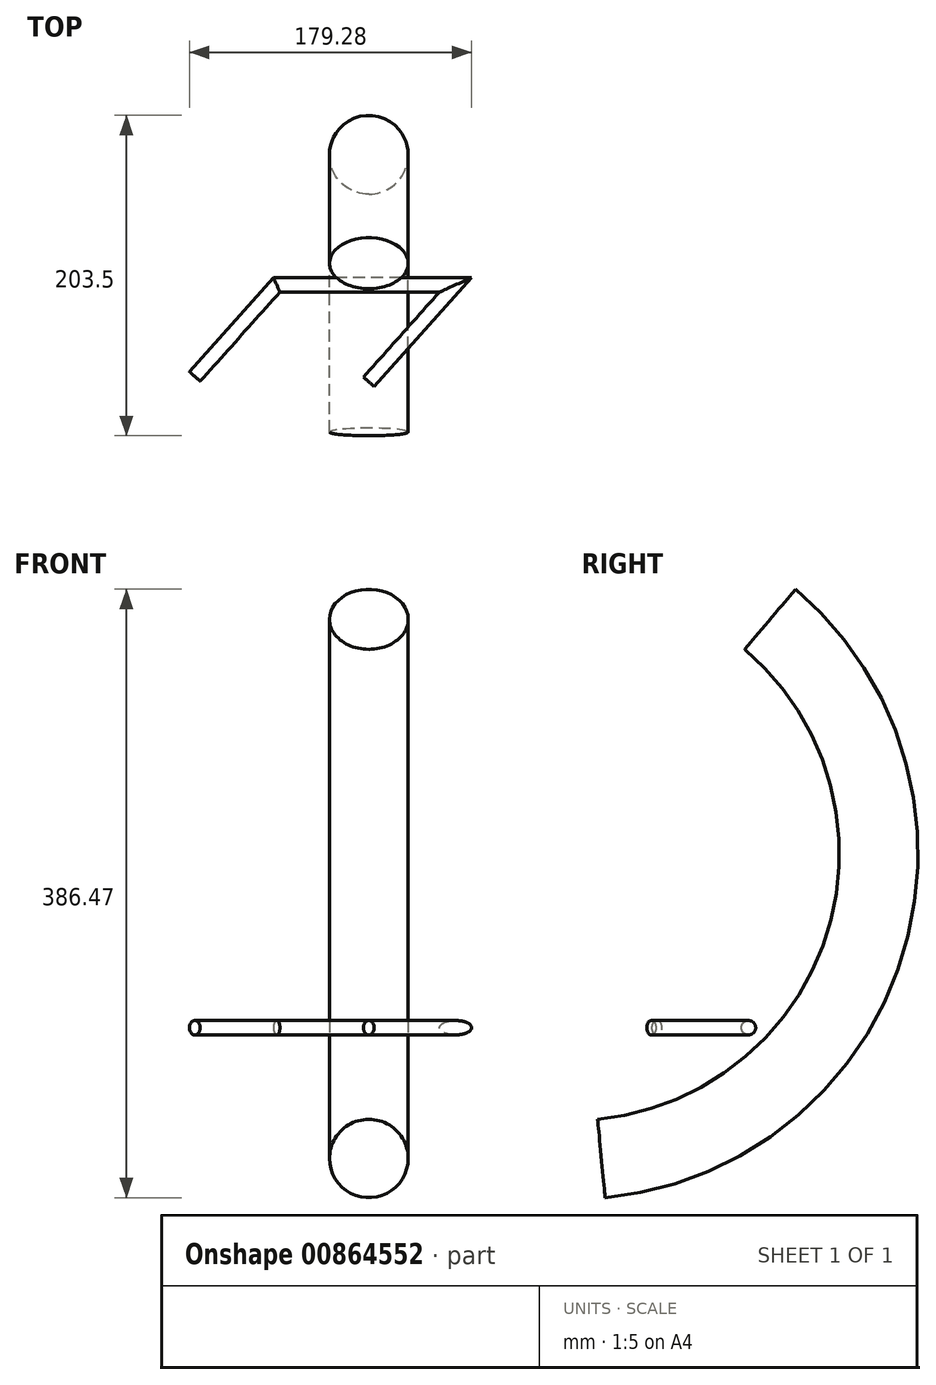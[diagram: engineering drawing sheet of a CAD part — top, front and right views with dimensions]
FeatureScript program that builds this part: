
annotation { "Feature Type Name" : "Feature", "Feature Type Description" : "" }
export const myFeature = defineFeature(function(context is Context, id is Id, definition is map)
    precondition{}
    {
        {
            var Q0;
            Q0=qCreatedBy(makeId("Top.planeOp"),FACE);
            var sketch = newSketch(context, id + "F0", { "sketchPlane" : qUnion([Q0])});
            skLineSegment(sketch, "E0", {"start": v(0, 0) * mm, "end": v(55.1, 61.61) * mm});
            skLineSegment(sketch, "E1", {"start": v(55.1, 61.61) * mm, "end": v(-58.5, 61.61) * mm});
            skLineSegment(sketch, "E2", {"start": v(-58.5, 61.61) * mm, "end": v(-110.54, 3.41) * mm});
            skSolve(sketch);
        }
        {
            var Q0;
            Q0=sQuery(id+"F0.wireOp",EDGE,"E2");
            cPlane(context, id + "F1", {"entities" : qUnion([Q0]), "cplaneType" : CPlaneType.MID_PLANE, "offset" : 25 * mm, "width" : 150 * mm, "height" : 150 * mm});
        }
        {
            var Q0;
            Q0=qCreatedBy(id+"F1.planeOp",FACE);
            var sketch = newSketch(context, id + "F2", { "sketchPlane" : qUnion([Q0])});
            skCircle(sketch, "E3", {"center": v(-84.67, 0) * mm, "radius": 4.58 * mm});
            skSolve(sketch);
        }
        {
            var Q0;
            Q0=makeQuery(id+"F2.imprint","IMPRINT",FACE,{"disambiguationData":[TD([[makeQuery(id+"F2.imprint","IMPRINT",EDGE,{"derivedFrom":sQuery(id+"F2.wireOp",EDGE,"E3")}),1.0]])]});
            var Q1;
            Q1=sQuery(id+"F0.wireOp",EDGE,"E2");
            var Q2;
            Q2=sQuery(id+"F0.wireOp",EDGE,"E1");
            var Q3;
            Q3=sQuery(id+"F0.wireOp",EDGE,"E0");
            sweep(context, id + "F3", {"profiles" : qUnion([Q0]), "path" : qUnion([Q1, Q2, Q3])});
        }
        {
            var Q0;
            Q0=qCreatedBy(makeId("Right.planeOp"),FACE);
            var sketch = newSketch(context, id + "F4", { "sketchPlane" : qUnion([Q0])});
            skArc(sketch, "E4", {"start": v(-31.83, -83.07) * mm, "mid": v(135.4, 52.62) * mm, "end": v(75.38, 259.44) * mm});
            skSolve(sketch);
        }
        {
            var Q0;
            Q0=sQuery(id+"F4.wireOp",EDGE,"E4");
            cPlane(context, id + "F5", {"entities" : qUnion([Q0]), "cplaneType" : CPlaneType.MID_PLANE, "offset" : 25 * mm, "width" : 150 * mm, "height" : 150 * mm});
        }
        {
            var Q0;
            Q0=qCreatedBy(id+"F5.planeOp",FACE);
            var sketch = newSketch(context, id + "F6", { "sketchPlane" : qUnion([Q0])});
            skCircle(sketch, "E5", {"center": v(0, 113.5) * mm, "radius": 25 * mm});
            skSolve(sketch);
        }
        {
            var Q0;
            Q0=makeQuery(id+"F6.imprint","IMPRINT",FACE,{"disambiguationData":[TD([[makeQuery(id+"F6.imprint","IMPRINT",EDGE,{"derivedFrom":sQuery(id+"F6.wireOp",EDGE,"E5")}),1.0]])]});
            var Q1;
            Q1=sQuery(id+"F4.wireOp",EDGE,"E4");
            sweep(context, id + "F7", {"profiles" : qUnion([Q0]), "path" : qUnion([Q1])});
        }
    });
